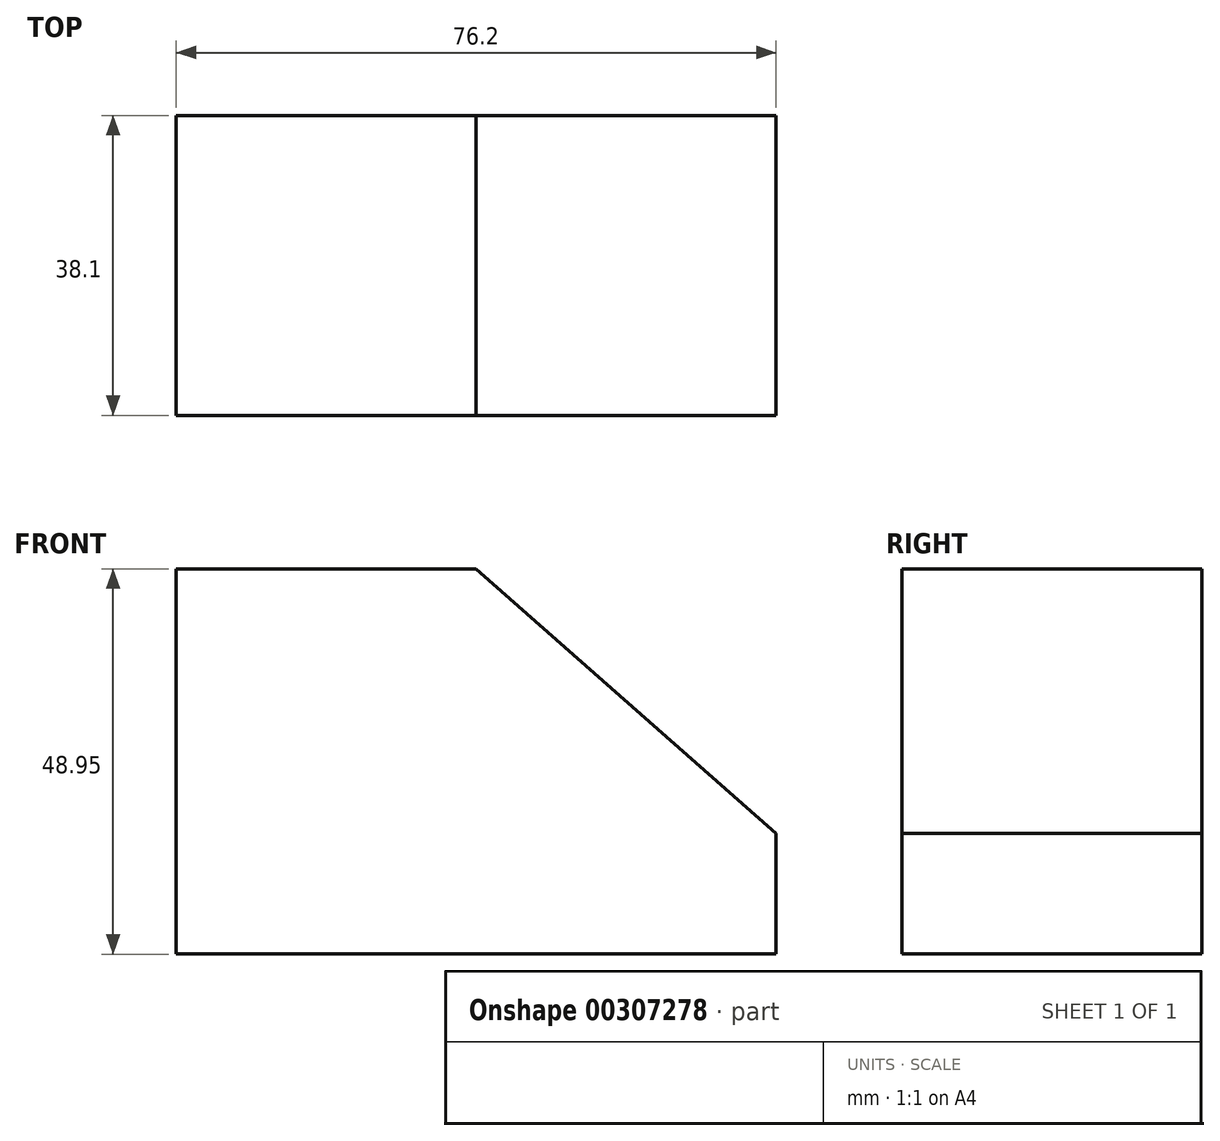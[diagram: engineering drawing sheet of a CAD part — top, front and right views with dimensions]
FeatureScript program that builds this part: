
annotation { "Feature Type Name" : "Feature", "Feature Type Description" : "" }
export const myFeature = defineFeature(function(context is Context, id is Id, definition is map)
    precondition{}
    {
        {
            var Q0;
            Q0=qCreatedBy(makeId("Front.planeOp"),FACE);
            var sketch = newSketch(context, id + "F0", { "sketchPlane" : qUnion([Q0])});
            skLineSegment(sketch, "E0", {"start": v(-43.49, -50.59) * mm, "end": v(32.71, -50.59) * mm});
            skLineSegment(sketch, "E1", {"start": v(32.71, -50.59) * mm, "end": v(32.71, -35.24) * mm});
            skLineSegment(sketch, "E2", {"start": v(32.71, -35.24) * mm, "end": v(-5.39, -1.64) * mm});
            skLineSegment(sketch, "E3", {"start": v(-5.39, -1.64) * mm, "end": v(-43.49, -1.64) * mm});
            skLineSegment(sketch, "E4", {"start": v(-43.49, -1.64) * mm, "end": v(-43.49, -50.59) * mm});
            skSolve(sketch);
        }
        {
            var Q0;
            Q0=makeQuery(id+"F0.imprint","IMPRINT",FACE,{"disambiguationData":[TD([[makeQuery(id+"F0.imprint","IMPRINT",EDGE,{"derivedFrom":sQuery(id+"F0.wireOp",EDGE,"E0")}),1.0]])]});
            extrude(context, id + "F1", {"entities" : qUnion([Q0]), "depth" : 38.1 * mm});
        }
    });
